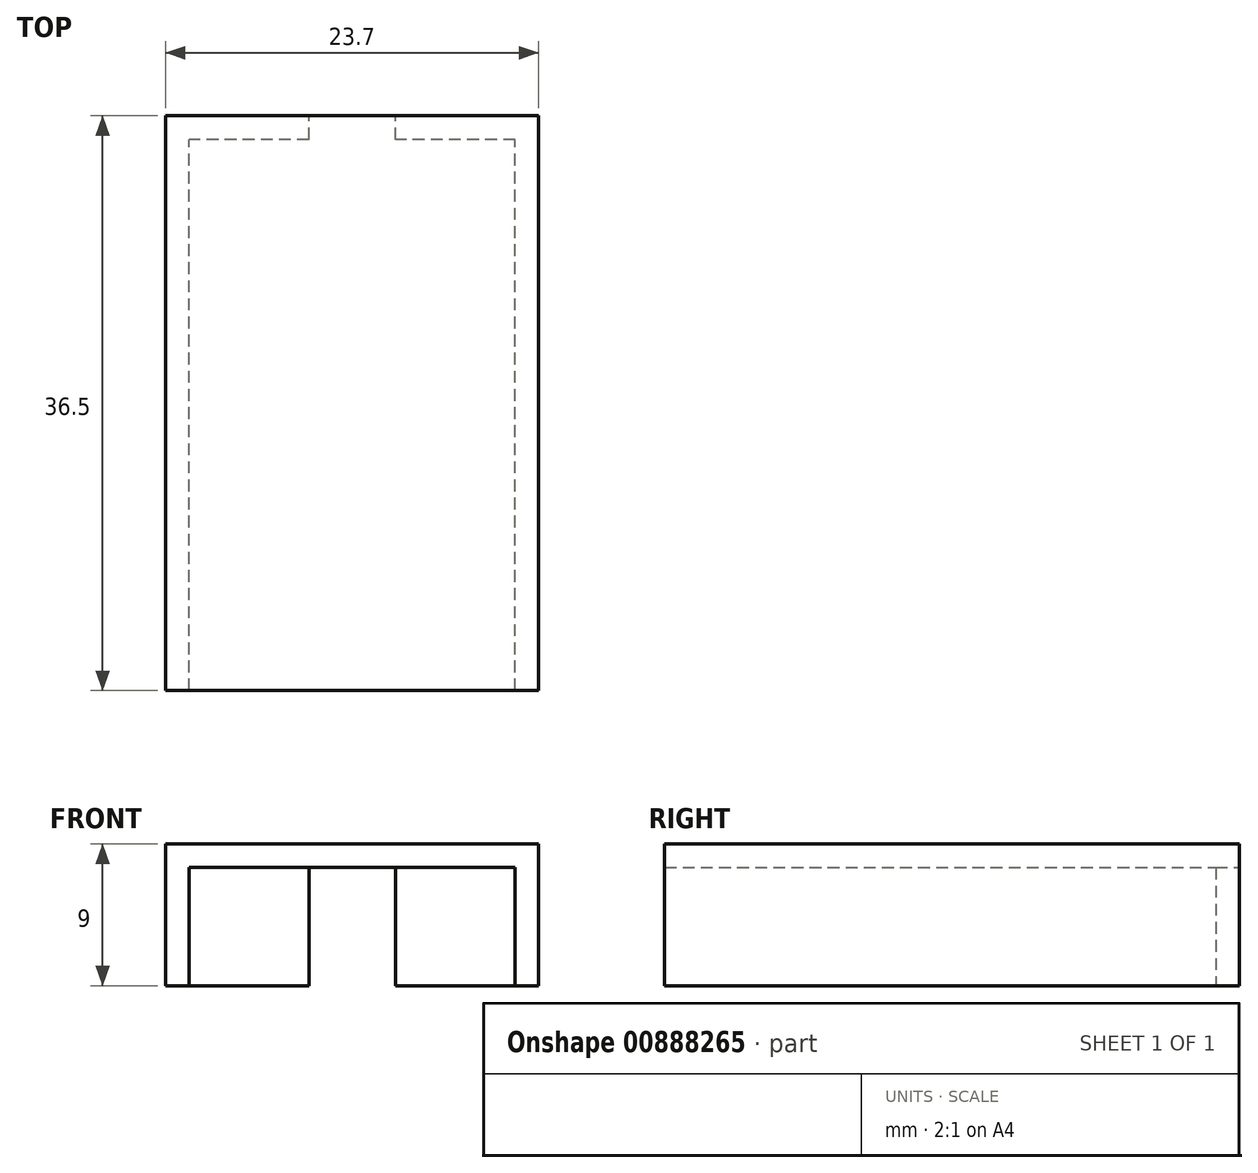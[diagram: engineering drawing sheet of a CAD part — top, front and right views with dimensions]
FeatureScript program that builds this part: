
annotation { "Feature Type Name" : "Feature", "Feature Type Description" : "" }
export const myFeature = defineFeature(function(context is Context, id is Id, definition is map)
    precondition{}
    {
        {
            var Q0;
            Q0=qCreatedBy(makeId("Top.planeOp"),FACE);
            var sketch = newSketch(context, id + "F0", { "sketchPlane" : qUnion([Q0])});
            skLineSegment(sketch, "E0.bottom", {"start": v(10.35, -17.5) * mm, "end": v(-10.35, -17.5) * mm});
            skLineSegment(sketch, "E0.top", {"start": v(10.35, 17.5) * mm, "end": v(2.75, 17.5) * mm});
            skLineSegment(sketch, "E0.left", {"start": v(10.35, -17.5) * mm, "end": v(10.35, 17.5) * mm});
            skLineSegment(sketch, "E0.right", {"start": v(-10.35, -17.5) * mm, "end": v(-10.35, 17.5) * mm});
            skPoint(sketch, "E0.middle", {"position": v(0, 0) * mm});
            skLineSegment(sketch, "E1.top", {"start": v(2.75, 19) * mm, "end": v(-2.75, 19) * mm});
            skLineSegment(sketch, "E1.left", {"start": v(2.75, 17.5) * mm, "end": v(2.75, 19) * mm});
            skLineSegment(sketch, "E1.right", {"start": v(-2.75, 17.5) * mm, "end": v(-2.75, 19) * mm});
            skPoint(sketch, "E1.middle", {"position": v(0, 17.5) * mm});
            skLineSegment(sketch, "E2.trimOffspring", {"start": v(-2.75, 17.5) * mm, "end": v(-10.35, 17.5) * mm});
            skPoint(sketch, "E1.bottom.end.orphan", {"position": v(-2.75, 16) * mm});
            skPoint(sketch, "E1.bottom.start.orphan", {"position": v(2.75, 16) * mm});
            skSolve(sketch);
        }
        {
            var Q0;
            Q0=qCreatedBy(makeId("Top.planeOp"),FACE);
            var sketch = newSketch(context, id + "F1", { "sketchPlane" : qUnion([Q0])});
            skLineSegment(sketch, "E3.0", {"start": v(11.85, -17.5) * mm, "end": v(11.85, 19) * mm});
            skLineSegment(sketch, "E4.0", {"start": v(11.85, 19) * mm, "end": v(-11.85, 19) * mm});
            skLineSegment(sketch, "E5.0", {"start": v(-11.85, -17.5) * mm, "end": v(-11.85, 19) * mm});
            skLineSegment(sketch, "E6", {"start": v(11.85, -17.5) * mm, "end": v(-11.85, -17.5) * mm});
            skSolve(sketch);
        }
        {
            var Q0;
            Q0 = qSketchRegion(id + "F1", true);
            extrude(context, id + "F2", {"entities" : qUnion([Q0]), "depth" : 9 * mm, "offsetDistance" : 25 * mm});
        }
        {
            var Q0;
            Q0 = qSketchRegion(id + "F0", true);
            extrude(context, id + "F3", {"entities" : qUnion([Q0]), "operationType" : NewBodyOperationType.REMOVE, "depth" : 7.5 * mm, "offsetDistance" : 25 * mm});
        }
    });
